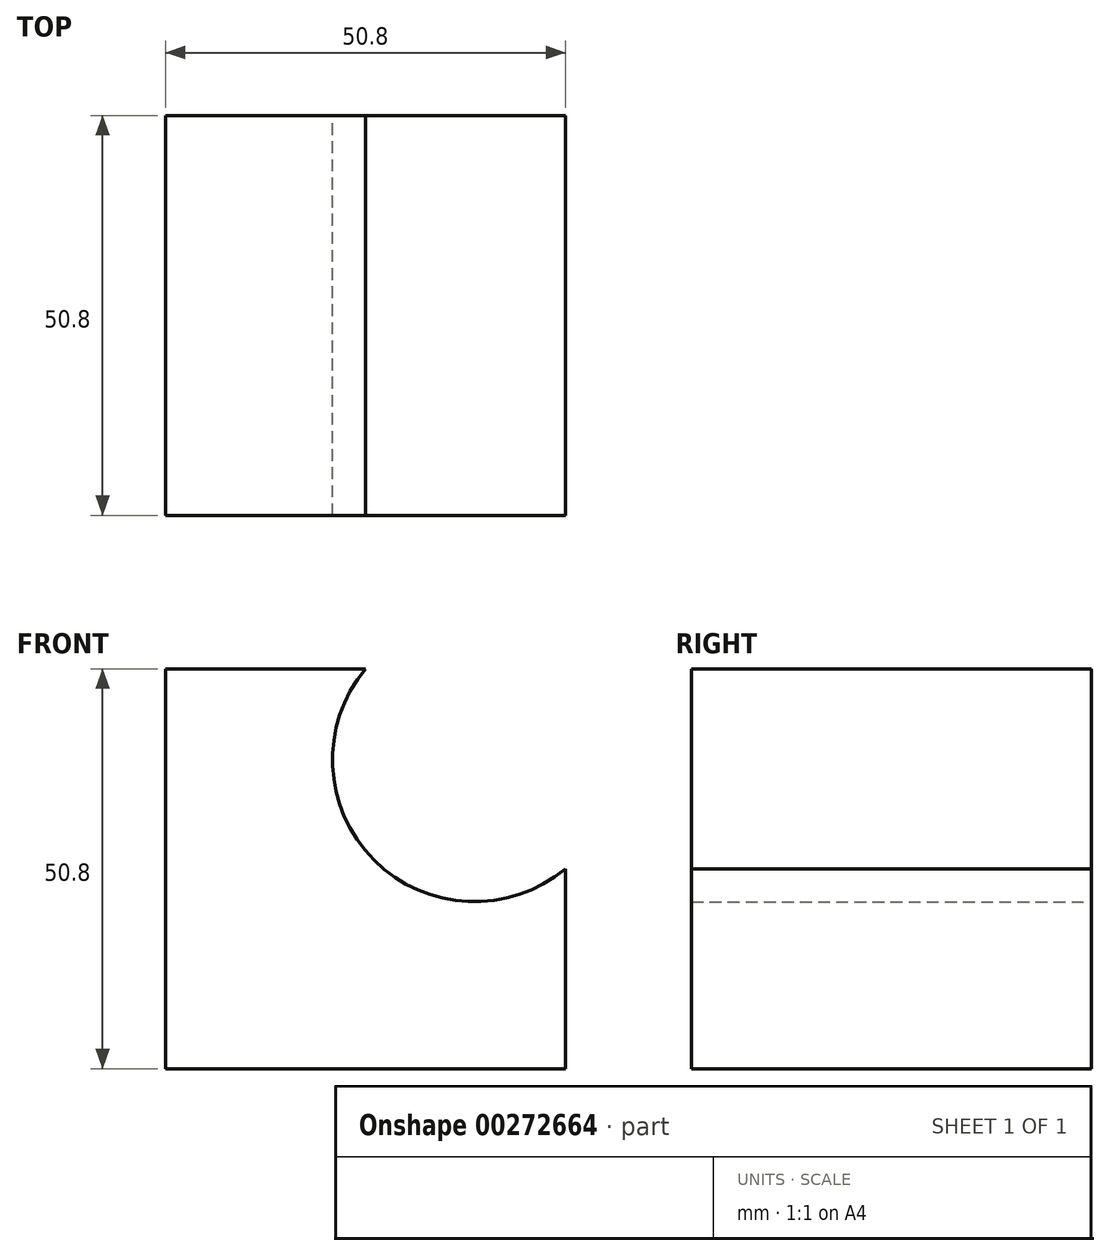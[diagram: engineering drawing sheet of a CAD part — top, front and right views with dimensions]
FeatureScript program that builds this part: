
annotation { "Feature Type Name" : "Feature", "Feature Type Description" : "" }
export const myFeature = defineFeature(function(context is Context, id is Id, definition is map)
    precondition{}
    {
        {
            var Q0;
            Q0=qCreatedBy(makeId("Front.planeOp"),FACE);
            var sketch = newSketch(context, id + "F0", { "sketchPlane" : qUnion([Q0])});
            skLineSegment(sketch, "E0", {"start": v(0, 0) * mm, "end": v(-50.8, 0) * mm});
            skLineSegment(sketch, "E1", {"start": v(-50.8, 0) * mm, "end": v(-50.8, 50.8) * mm});
            skLineSegment(sketch, "E2", {"start": v(-50.8, 50.8) * mm, "end": v(-25.4, 50.8) * mm});
            skLineSegment(sketch, "E3", {"start": v(0, 0) * mm, "end": v(0, 25.4) * mm});
            skArc(sketch, "E4", {"start": v(-25.4, 50.8) * mm, "mid": v(-24.3, 26.5) * mm, "end": v(0, 25.4) * mm});
            skSolve(sketch);
        }
        {
            var Q0;
            Q0=makeQuery(id+"F0.imprint","IMPRINT",FACE,{"disambiguationData":[TD([[makeQuery(id+"F0.imprint","IMPRINT",EDGE,{"derivedFrom":sQuery(id+"F0.wireOp",EDGE,"E0")}),-1.0]])]});
            extrude(context, id + "F1", {"entities" : qUnion([Q0]), "depth" : 50.8 * mm});
        }
    });
